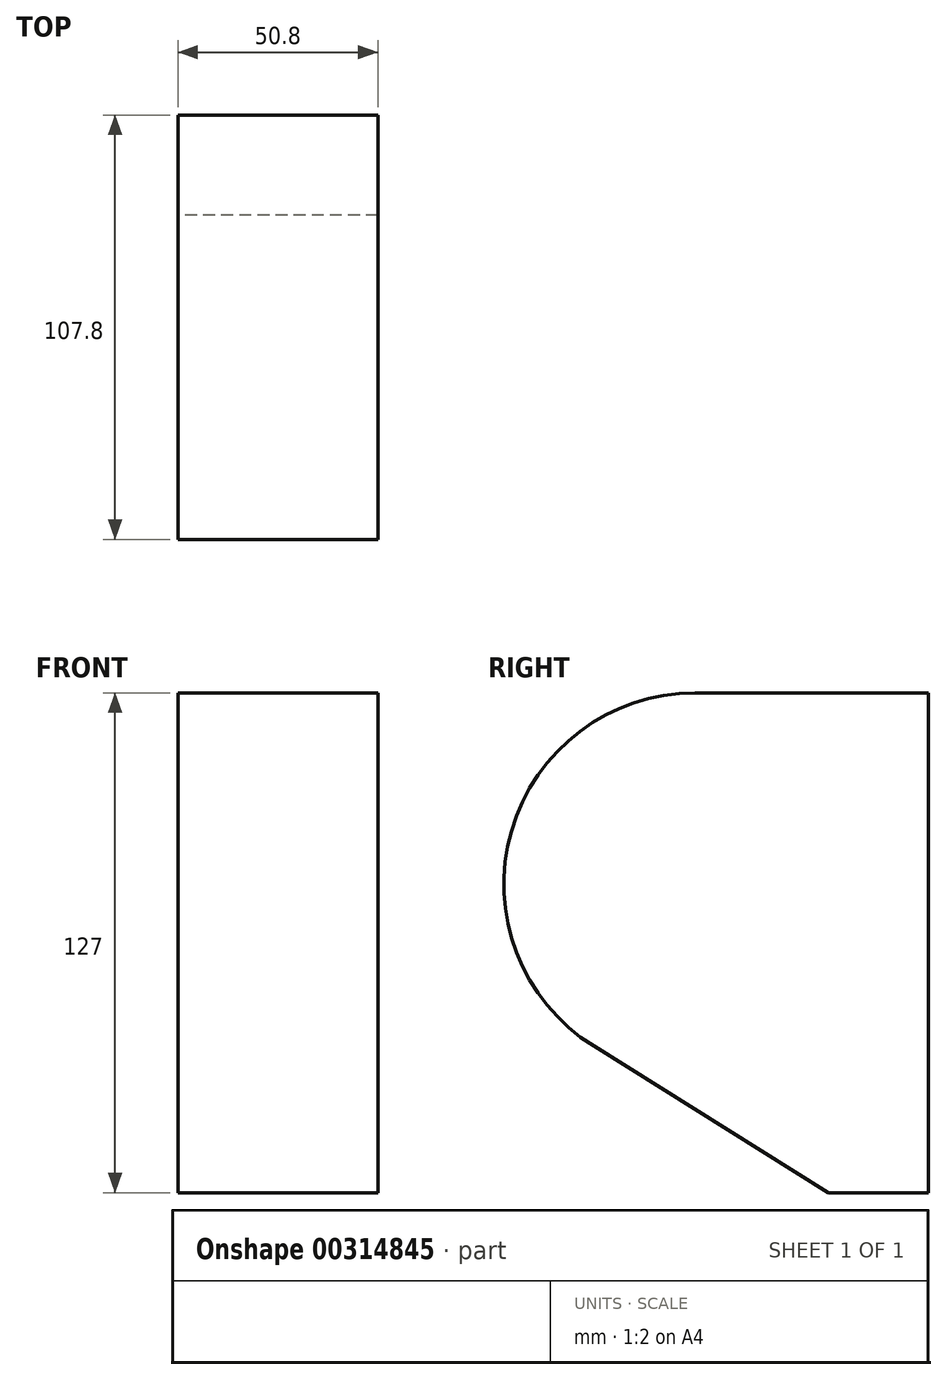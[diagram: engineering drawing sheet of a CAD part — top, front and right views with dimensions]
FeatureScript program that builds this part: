
annotation { "Feature Type Name" : "Feature", "Feature Type Description" : "" }
export const myFeature = defineFeature(function(context is Context, id is Id, definition is map)
    precondition{}
    {
        {
            var Q0;
            Q0=qCreatedBy(makeId("Top.planeOp"),FACE);
            var sketch = newSketch(context, id + "F0", { "sketchPlane" : qUnion([Q0])});
            skLineSegment(sketch, "E0.bottom", {"start": v(0, 0.5) * mm, "end": v(50.8, 0.5) * mm});
            skLineSegment(sketch, "E0.top", {"start": v(0, 127.5) * mm, "end": v(50.8, 127.5) * mm});
            skLineSegment(sketch, "E0.left", {"start": v(0, 0.5) * mm, "end": v(0, 127.5) * mm});
            skLineSegment(sketch, "E0.right", {"start": v(50.8, 0.5) * mm, "end": v(50.8, 127.5) * mm});
            skSolve(sketch);
        }
        {
            var Q0;
            Q0 = qSketchRegion(id + "F0", true);
            extrude(context, id + "F1", {"entities" : qUnion([Q0]), "depth" : 127 * mm});
        }
        {
            var Q0;
            Q0=makeQuery(id+"F1.opExtrude","CAP_EDGE",EDGE,{"disambiguationData":[OSD([sQuery(id+"F0.wireOp",EDGE,"E0.bottom")])],"isStart":false});
            fillet(context, id + "F2", {"entities" : qUnion([Q0]), "radius" : 63.5 * mm, "tangentPropagation" : true, "allowEdgeOverflow" : false});
        }
        {
            var Q0;
            Q0=makeQuery(id+"F1.opExtrude","CAP_EDGE",EDGE,{"disambiguationData":[OSD([sQuery(id+"F0.wireOp",EDGE,"E0.bottom")])],"isStart":true});
            chamfer(context, id + "F3", {"entities" : qUnion([Q0]), "chamferType" : ChamferType.TWO_OFFSETS, "width1" : 63.5 * mm, "oppositeDirection" : false, "width2" : 101.6 * mm, "tangentPropagation" : true});
        }
        {
            var Q0;
            {var subQ0=sQuery(id+"F0.wireOp",EDGE,"E0.bottom");Q0=makeQuery(id+"F3.opChamfer","BLEND_EDGE",EDGE,{"blendedFrom":[makeQuery(id+"F1.opExtrude","CAP_EDGE",EDGE,{"disambiguationData":[OSD([subQ0])],"isStart":true}),makeQuery(id+"F2.opFillet","BLEND_FACE",FACE,{"disambiguationData":[OSD([subQ0])]})],"blendedInto":[makeQuery(id+"F2.opFillet","BLEND_FACE",FACE,{"disambiguationData":[OSD([subQ0])]})]});}
            fillet(context, id + "F4", {"entities" : qUnion([Q0]), "radius" : 48.58 * mm, "tangentPropagation" : true, "allowEdgeOverflow" : false});
        }
    });
